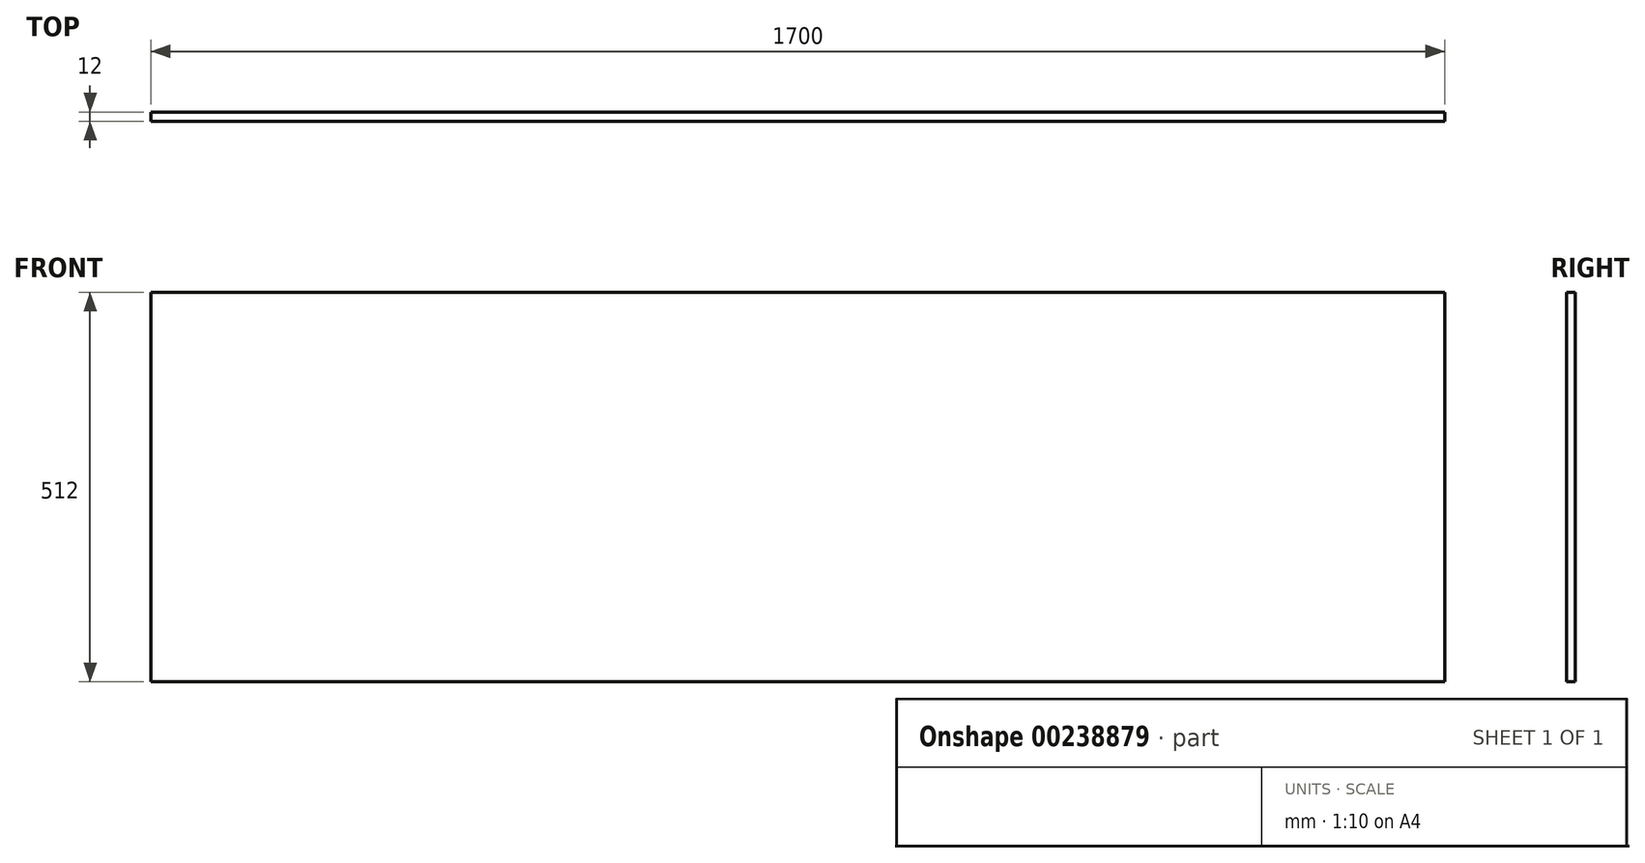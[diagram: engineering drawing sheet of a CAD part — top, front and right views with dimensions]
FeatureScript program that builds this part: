
annotation { "Feature Type Name" : "Feature", "Feature Type Description" : "" }
export const myFeature = defineFeature(function(context is Context, id is Id, definition is map)
    precondition{}
    {
        {
            var Q0;
            Q0=qCreatedBy(makeId("Front.planeOp"),FACE);
            var sketch = newSketch(context, id + "F0", { "sketchPlane" : qUnion([Q0])});
            skLineSegment(sketch, "E0.bottom", {"start": v(0, 0) * mm, "end": v(1700, 0) * mm});
            skLineSegment(sketch, "E0.top", {"start": v(0, 512) * mm, "end": v(1700, 512) * mm});
            skLineSegment(sketch, "E0.left", {"start": v(0, 0) * mm, "end": v(0, 512) * mm});
            skLineSegment(sketch, "E0.right", {"start": v(1700, 0) * mm, "end": v(1700, 512) * mm});
            skSolve(sketch);
        }
        {
            var Q0;
            Q0=makeQuery(id+"F0.imprint","IMPRINT",FACE,{"disambiguationData":[TD([[makeQuery(id+"F0.imprint","IMPRINT",EDGE,{"derivedFrom":sQuery(id+"F0.wireOp",EDGE,"E0.bottom")}),1.0]])]});
            extrude(context, id + "F1", {"entities" : qUnion([Q0]), "offsetDistance" : 25 * mm, "depth" : 12 * mm});
        }
    });
